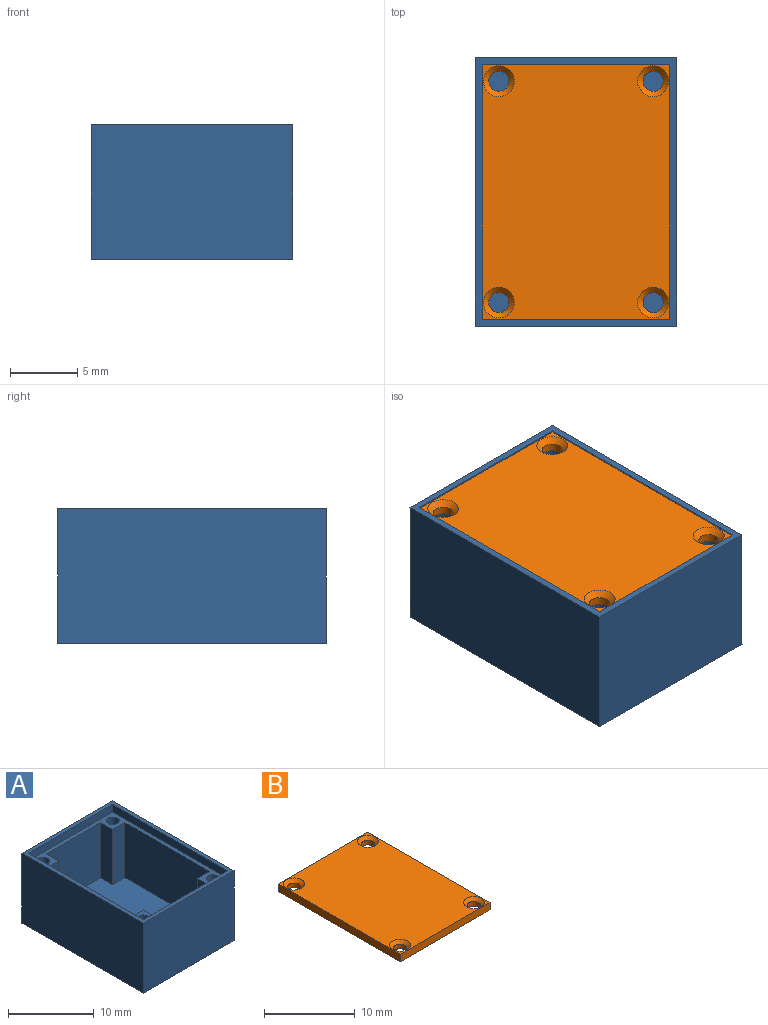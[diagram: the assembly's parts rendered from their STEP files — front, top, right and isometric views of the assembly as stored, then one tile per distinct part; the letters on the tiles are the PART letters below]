
ASSEMBLY  parts=2 mates=1
PART A: 32 faces, bbox 15x20x10 mm
  f0: plane 18x13mm, normal (0,0,1), area 218mm2, adj f1,f2,f3,f4,f16,f17,f18,f19
  f1: plane 9x7.9mm, normal (0,1,0), area 71.1mm2, adj f0,f15,f21,f23
  f2: plane 9x7.9mm, normal (0,-1,0), area 71.1mm2, adj f0,f15,f17,f18
  f3: plane 14x7.9mm, normal (-1,0,0), area 110.6mm2, adj f0,f15,f19,f20
  f4: plane 14x7.9mm, normal (1,0,0), area 110.6mm2, adj f0,f15,f16,f22
  f5: plane 20x15mm, normal (0,0,1), area 34mm2, adj f6,f7,f8,f9,f11,f12,f13,f14
  f6: plane 20x10mm, normal (1,0,0), area 200mm2, adj f5,f7,f9,f10
  f7: plane 15x10mm, normal (0,1,0), area 150mm2, adj f5,f6,f8,f10
  f8: plane 20x10mm, normal (-1,0,0), area 200mm2, adj f5,f7,f9,f10
  f9: plane 15x10mm, normal (0,-1,0), area 150mm2, adj f5,f6,f8,f10
  f10: plane 20x15mm, normal (0,0,-1), area 300mm2, adj f6,f7,f8,f9
  f11: plane 19x1.1mm, normal (1,0,0), area 20.9mm2, adj f5,f12,f14,f15
  f12: plane 14x1.1mm, normal (0,1,0), area 15.4mm2, adj f5,f11,f13,f15
  f13: plane 19x1.1mm, normal (-1,0,0), area 20.9mm2, adj f5,f12,f14,f15
  f14: plane 14x1.1mm, normal (0,-1,0), area 15.4mm2, adj f5,f11,f13,f15
  f15: plane 19x14mm, normal (0,0,1), area 40.9mm2, adj f1,f2,f3,f4,f11,f12,f13,f14
  f16: plane 7.9x2mm, normal (0,-1,0), area 15.8mm2, adj f0,f4,f15,f17
  f17: plane 7.9x2mm, normal (1,0,0), area 15.8mm2, adj f0,f2,f15,f16
  f18: plane 7.9x2mm, normal (-1,0,0), area 15.8mm2, adj f0,f2,f15,f19
  f19: plane 7.9x2mm, normal (0,-1,0), area 15.8mm2, adj f0,f3,f15,f18
  f20: plane 7.9x2mm, normal (0,1,0), area 15.8mm2, adj f0,f3,f15,f21
  f21: plane 7.9x2mm, normal (-1,0,0), area 15.8mm2, adj f0,f1,f15,f20
  f22: plane 7.9x2mm, normal (0,1,0), area 15.8mm2, adj f0,f4,f15,f23
  f23: plane 7.9x2mm, normal (1,0,0), area 15.8mm2, adj f0,f1,f15,f22
  f24: cylinder r=0.75mm len=5mm, axis (0,0,1), area 23.6mm2, adj f15,f25
  f25: plane 1.5x1.5mm, normal (0,0,1), area 1.8mm2, adj f24
  f26: cylinder r=0.75mm len=5mm, axis (0,0,1), area 23.6mm2, adj f15,f27
  f27: plane 1.5x1.5mm, normal (0,0,1), area 1.8mm2, adj f26
  f28: cylinder r=0.75mm len=5mm, axis (0,0,1), area 23.6mm2, adj f15,f29
  f29: plane 1.5x1.5mm, normal (0,0,1), area 1.8mm2, adj f28
  f30: cylinder r=0.75mm len=5mm, axis (0,0,1), area 23.6mm2, adj f15,f31
  f31: plane 1.5x1.5mm, normal (0,0,1), area 1.8mm2, adj f30
PART B: 14 faces, bbox 14x19x1 mm
  f0: plane 19x1mm, normal (-1,0,0), area 19mm2, adj f1,f6,f8,f9
  f1: plane 14x1mm, normal (0,-1,0), area 14mm2, adj f0,f2,f8,f9
  f2: plane 19x1mm, normal (1,0,0), area 19mm2, adj f1,f6,f8,f9
  f3: cylinder r=0.75mm len=1.5mm, axis (0,0,-1), area 2.8mm2, adj f9,f13
  f4: cylinder r=0.75mm len=1.5mm, axis (0,0,-1), area 2.8mm2, adj f9,f10
  f5: cylinder r=0.75mm len=1.5mm, axis (0,0,-1), area 2.8mm2, adj f9,f11
  f6: plane 14x1mm, normal (0,1,0), area 14mm2, adj f0,f2,f8,f9
  f7: cylinder r=0.75mm len=1.5mm, axis (0,0,-1), area 2.8mm2, adj f9,f12
  f8: plane 19x14mm, normal (0,0,1), area 249.4mm2, adj f0,f1,f2,f6,f10,f11,f12,f13
  f9: plane 19x14mm, normal (0,0,-1), area 258.9mm2, adj f0,f1,f2,f3,f4,f5,f6,f7
  f10: cone r=0.75mm half-angle=45deg, axis (0,0,1), area 3.4mm2, adj f4,f8
  f11: cone r=0.75mm half-angle=45deg, axis (0,0,1), area 3.4mm2, adj f5,f8
  f12: cone r=0.75mm half-angle=45deg, axis (0,0,1), area 3.4mm2, adj f7,f8
  f13: cone r=0.75mm half-angle=45deg, axis (0,0,1), area 3.4mm2, adj f3,f8
PLACE A t=(-10.33,-36.04,4.82)mm
PLACE B rot(axis=(-0.73,0.28,0.63),0deg) t=(-9.77,36.67,13.72)mm
MATE slider A.f30 <-> B.f4  axis (0,0,1) through (33.26,13.02,13.72)mm
